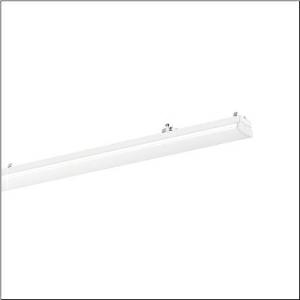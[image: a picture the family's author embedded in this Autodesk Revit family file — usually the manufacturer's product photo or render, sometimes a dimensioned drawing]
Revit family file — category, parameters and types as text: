
# Revit family: licross_21_recessed_opal_mo_52te1dvn465g
name_source: partatom
category: Lighting Fixtures
units: mm (PartAtom-declared; Revit-internal decimal feet)

## family parameters
Cut with Voids When Loaded = No
Host = Face
Light Source = No
Part Type = Normal
Room Calculation Point = No
Round Connector Dimension = Use Diameter
Shared = No

## types (1)
- --- (1 x LED, 6500 lm, 37.7 W, 4000K)
    Apparent Load = 38 VA
    CIE Flux Codes = 44 73 91 87 100
    Color Rendering = 80
    Color Temperature = 4000K
    Default Elevation = 1800 mm
    Description = Licross 21 recessed opal MO, luminaire insert, of sheet steel, galvanised, coil coated, white, length: 1.500mm, width: 66mm, height: 67mm, LED rated luminous flux: 6.500lm, light colour: 840, SDCM (Standard Deviation of Colour Matching)MacAdam ≤ 3 SDCM (initial), control gear: DALI 2, CLO, with plug, 5-pole, with phase selection, mains connection: 220..240V, AC, 50/60Hz, start of lifetime: 38W, end of service life: 45W, internal wiring halogen-free, primary optical cover: cover, of PMMA, light emission: direct with ceiling illumination distribution, primary light characteristic: symmetric, protection rating (complete): IP54, insulation class (complete): insulation class I (protective earthing), certification: CE, ENEC, VDE, UKCA, protection symbol: D if used in an environment with non-conductive dust loads with corresponding accessories, impact resistance: IK06, permissible ambient temperature for indoor applications: -25..+40°C, corresponds to IFS (International Featured Standards) requirements for safety and quality in the food industry, reducing of maximum allowable ambient temperature of 5°C with ceiling mounting, LABS conformity tested according to VDMA 24364:2018-05, The light source and the operating device comply with the requirements of the Ecodesign Regulation (EU) 2019/2020 and are replaceable in accordance with this regulation, packaging unit: 1 piece
    Height = 83 mm
    Lamp = 1 x LED
    Lamp Light Flux = 6500 lm
    Lamp Power = 37.7 W
    Lamp count = 1
    Length = 1500 mm
    Luminous efficacy = 172 lm/W
    Manufacturer = Siteco
    ModVariant = No
    Model = 52TE1DVN465G
    Mounting Place = Ceiling
    Mounting Type = Pendant
    Number of Poles = 1
    OnlyDefault = Yes
    Power Factor = 1
    Product Name = Licross 21 recessed opal MO
    Product group = luminaire insert | ceiling pendant
    ProductGroupID = 901
    Protection Class = Protection class I
    Protection Degree = IP 54
    RLX_Detail_Level = 1
    RLX_Emergency_Light_Flux = 0 lm
    RLX_Emergency_Type = 0
    RLX_Emergency_Type_DB = No
    RlxData = <blob elided: 27241 chars, md5=f6e14e42>
    Socket = socket
    Standby Power = 0 W
    System Light Flux = 6500 lm
    System Power = 38 W
    Type Comments = factory setting: luminous flux: 100 % | dim-lin: 254 | 252 mA
    Type Image = l_1313666.jpg
    URL = http://relux.com
    VarID = @adj_076043
    Voltage = 0 V
    Weight = 0.00 kg
    Width = 76 mm

## geometry (parser evidence)
native form markers: Blend x4, Sweep x13
no freeform markers — native parametric forms only
